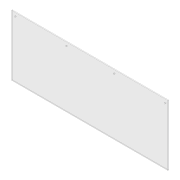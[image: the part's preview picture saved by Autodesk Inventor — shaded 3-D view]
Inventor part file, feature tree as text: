
AUTODESK INVENTOR PART (.ipt)
format: ipt  version: 2012 (Build 160160000, 160)  size: 79,872 bytes
history: native  units: in
note: dims shown in document units (in); Inventor stores cm internally (conversion verified against a paired STEP export)
features: extrude x1, sketch x1
ambient origin geometry x8: Origin, YZ Plane, XZ Plane, XY Plane, X Axis, Y Axis, Z Axis, Center Point
bodies: Solid1 (feature_tree)
feature tree (2):
  extrude  "Extrusion1"  Depth=49.0in
  sketch  "Sketch1"  dims[d0=19.0in d1=49.0in d2=0.375in d3=0.375in d4=0.375in d5=0.375in d6=1.0in d7=17.0in d8=32.0in d9=48.0in d10=0.25in d11=0.0in d12=1.25in d13=1.25in d14=1.25in d15=1.25in]
